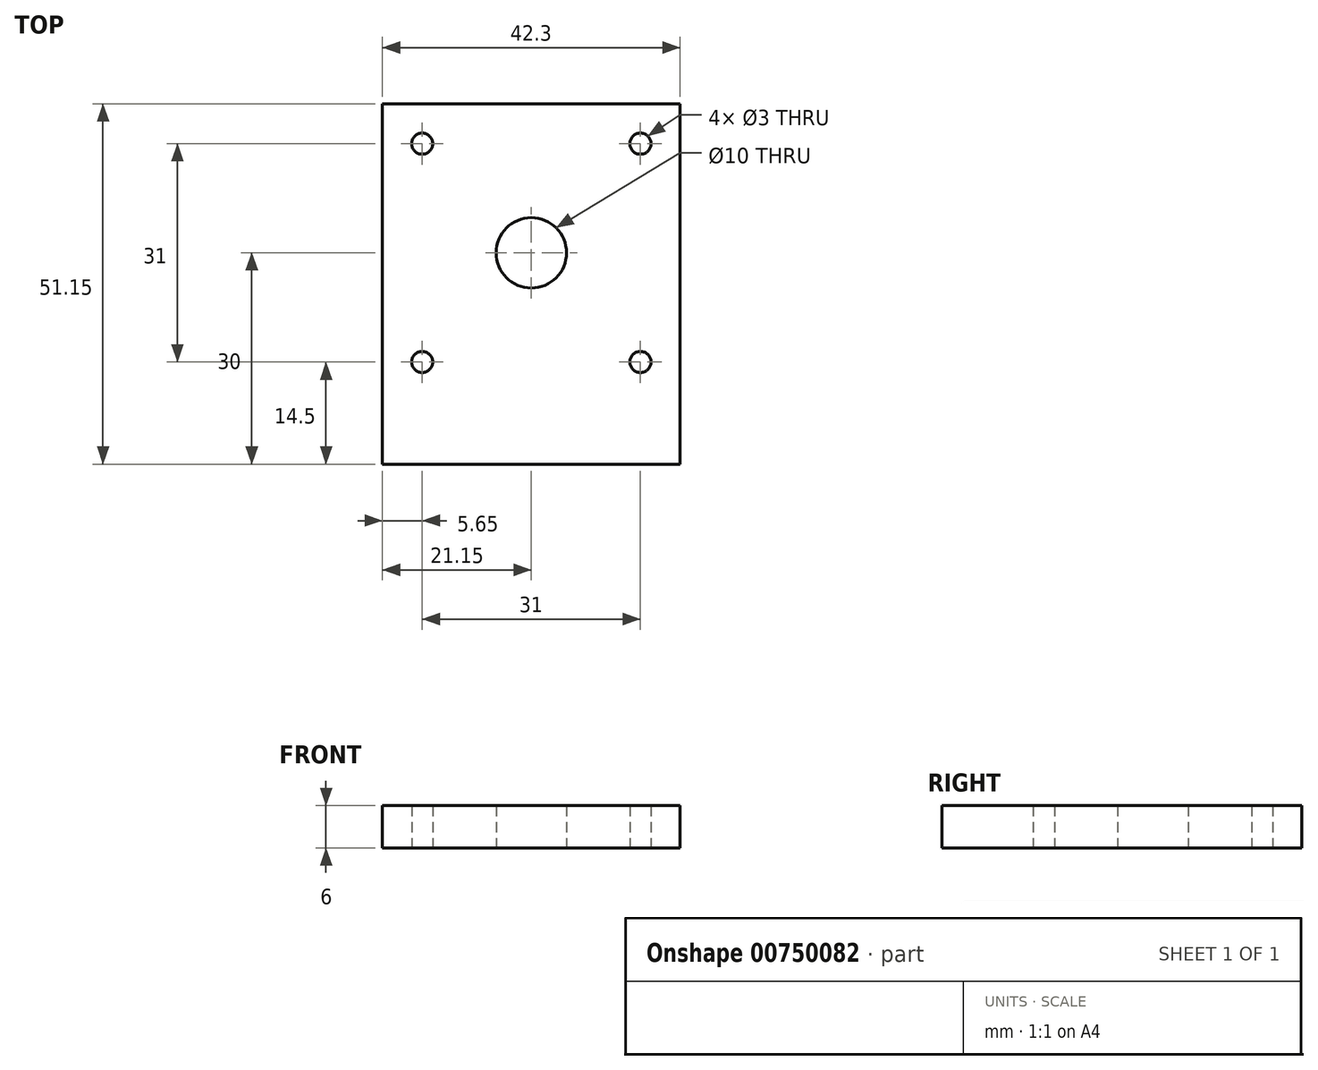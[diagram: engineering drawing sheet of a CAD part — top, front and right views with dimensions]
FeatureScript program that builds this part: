
annotation { "Feature Type Name" : "Feature", "Feature Type Description" : "" }
export const myFeature = defineFeature(function(context is Context, id is Id, definition is map)
    precondition{}
    {
        {
            var Q0;
            Q0=qCreatedBy(makeId("Top.planeOp"),FACE);
            var sketch = newSketch(context, id + "F0", { "sketchPlane" : qUnion([Q0])});
            skCircle(sketch, "E0", {"center": v(0, 0) * mm, "radius": 5 * mm});
            skCircle(sketch, "E1", {"center": v(-15.5, 15.5) * mm, "radius": 1.5 * mm});
            skLineSegment(sketch, "E2.bottom", {"start": v(-21.15, 21.15) * mm, "end": v(21.15, 21.15) * mm});
            skLineSegment(sketch, "E2.top", {"start": v(-21.15, -30) * mm, "end": v(21.15, -30) * mm});
            skLineSegment(sketch, "E2.left", {"start": v(-21.15, 21.15) * mm, "end": v(-21.15, -30) * mm});
            skLineSegment(sketch, "E2.right", {"start": v(21.15, 21.15) * mm, "end": v(21.15, -30) * mm});
            skCircle(sketch, "E3", {"center": v(15.5, 15.5) * mm, "radius": 1.5 * mm});
            skCircle(sketch, "E4", {"center": v(15.5, -15.5) * mm, "radius": 1.5 * mm});
            skCircle(sketch, "E5", {"center": v(-15.5, -15.5) * mm, "radius": 1.5 * mm});
            skSolve(sketch);
        }
        {
            var Q0;
            Q0=makeQuery(id+"F0.imprint","IMPRINT",FACE,{"disambiguationData":[TD([[makeQuery(id+"F0.imprint","IMPRINT",EDGE,{"derivedFrom":sQuery(id+"F0.wireOp",EDGE,"E0")}),-1.0]])]});
            extrude(context, id + "F1", {"entities" : qUnion([Q0]), "depth" : 6 * mm, "offsetDistance" : 25 * mm});
        }
    });
